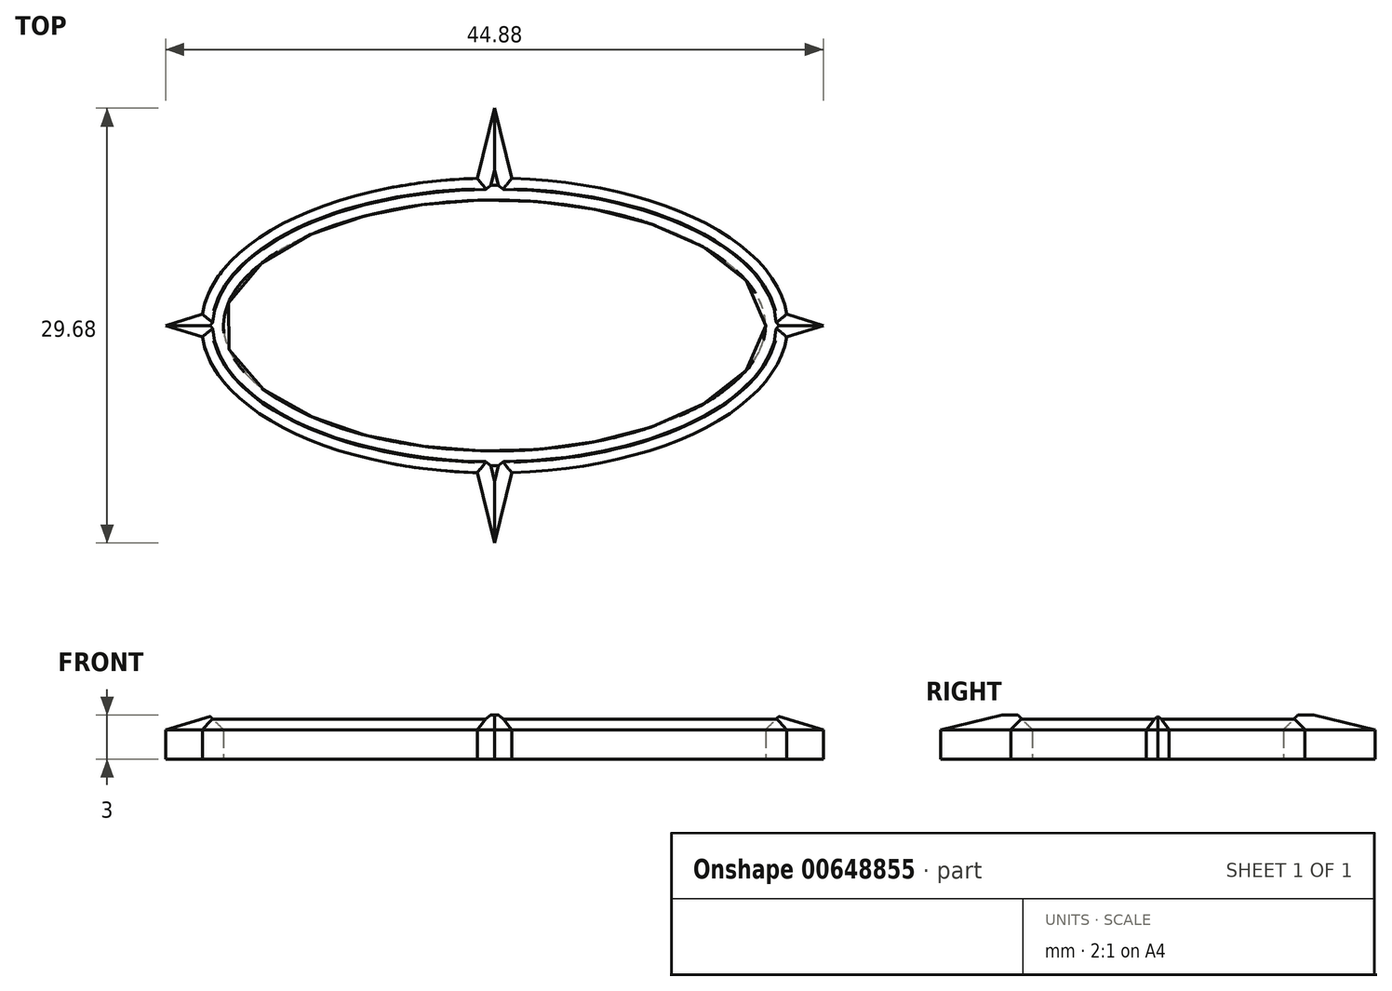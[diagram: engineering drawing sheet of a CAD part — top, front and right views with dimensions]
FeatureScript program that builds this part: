
annotation { "Feature Type Name" : "Feature", "Feature Type Description" : "" }
export const myFeature = defineFeature(function(context is Context, id is Id, definition is map)
    precondition{}
    {
        {
            var Q0;
            Q0=qCreatedBy(makeId("Top.planeOp"),FACE);
            var sketch = newSketch(context, id + "F0", { "sketchPlane" : qUnion([Q0])});
            skEllipse(sketch, "E0", {"center": v(0, 0) * mm, "majorRadius": 20 * mm, "minorRadius": 10.06 * mm, "majorAxis": v(-1, 0)});
            skSolve(sketch);
        }
        {
            var Q0;
            Q0=makeQuery(id+"F0.imprint","IMPRINT",FACE,{"disambiguationData":[TD([[makeQuery(id+"F0.imprint","IMPRINT",EDGE,{"derivedFrom":sQuery(id+"F0.wireOp",EDGE,"E0")}),1.0]])]});
            extrude(context, id + "F1", {"entities" : qUnion([Q0]), "depth" : 3 * mm, "offsetDistance" : 25 * mm});
        }
        {
            var Q0;
            Q0=makeQuery(id+"F1.opExtrude","CAP_FACE",FACE,{"disambiguationData":[OSD([sQuery(id+"F0.wireOp",EDGE,"E0")])],"isStart":false});
            shell(context, id + "F2", {"entities" : qUnion([Q0]), "thickness" : 1.5 * mm});
        }
        {
            var Q0;
            {var subQ0=sQuery(id+"F0.wireOp",EDGE,"E0");Q0=makeQuery(id+"F2.opShell","OFFSET_FACE",FACE,{"disambiguationData":[OSD([subQ0]),TDD([makeQuery(id+"F1.opExtrude","CAP_FACE",FACE,{"disambiguationData":[OSD([subQ0])],"isStart":true})])]});}
            extrude(context, id + "F3", {"entities" : qUnion([Q0]), "operationType" : NewBodyOperationType.REMOVE, "oppositeDirection" : true, "depth" : 25 * mm, "offsetDistance" : 25 * mm});
        }
        {
            var Q0;
            Q0=qCreatedBy(makeId("Top.planeOp"),FACE);
            var sketch = newSketch(context, id + "F4", { "sketchPlane" : qUnion([Q0])});
            skLineSegment(sketch, "E1", {"start": v(0, 9.84) * mm, "end": v(0, 14.84) * mm});
            skLineSegment(sketch, "E2", {"start": v(0, 14.84) * mm, "end": v(-1.22, 9.84) * mm});
            skLineSegment(sketch, "E3", {"start": v(-1.22, 9.84) * mm, "end": v(0, 9.84) * mm});
            skSolve(sketch);
        }
        {
            var Q0;
            Q0=makeQuery(id+"F4.imprint","IMPRINT",FACE,{"disambiguationData":[TD([[makeQuery(id+"F4.imprint","IMPRINT",EDGE,{"derivedFrom":sQuery(id+"F4.wireOp",EDGE,"E1")}),1.0]])]});
            extrude(context, id + "F5", {"entities" : qUnion([Q0]), "operationType" : NewBodyOperationType.ADD, "depth" : 3 * mm, "offsetDistance" : 25 * mm});
        }
        {
            var Q0;
            Q0=qCreatedBy(makeId("Top.planeOp"),FACE);
            var sketch = newSketch(context, id + "F6", { "sketchPlane" : qUnion([Q0])});
            skLineSegment(sketch, "E4", {"start": v(-19.97, 0) * mm, "end": v(-22.44, 0) * mm});
            skLineSegment(sketch, "E5", {"start": v(-22.44, 0) * mm, "end": v(-19.85, 0.8) * mm});
            skLineSegment(sketch, "E6", {"start": v(-19.85, 0.8) * mm, "end": v(-19.97, 0) * mm});
            skSolve(sketch);
        }
        {
            var Q0;
            Q0=makeQuery(id+"F6.imprint","IMPRINT",FACE,{"disambiguationData":[TD([[makeQuery(id+"F6.imprint","IMPRINT",EDGE,{"derivedFrom":sQuery(id+"F6.wireOp",EDGE,"E4")}),-1.0]])]});
            extrude(context, id + "F7", {"entities" : qUnion([Q0]), "operationType" : NewBodyOperationType.ADD, "depth" : 3 * mm, "offsetDistance" : 25 * mm});
        }
        {
            var Q0;
            Q0=makeQuery(id+"F1.opExtrude","SWEPT_BODY",BODY,{"disambiguationData":[OSD([sQuery(id+"F0.wireOp",EDGE,"E0")])]});
            var Q1;
            Q1=qCreatedBy(makeId("Right.planeOp"),FACE);
            mirror(context, id + "F8", {"operationType" : NewBodyOperationType.ADD, "entities" : qUnion([Q0]), "mirrorPlane" : qUnion([Q1])});
        }
        {
            var Q0;
            Q0=makeQuery(id+"F1.opExtrude","SWEPT_BODY",BODY,{"disambiguationData":[OSD([sQuery(id+"F0.wireOp",EDGE,"E0")])]});
            var Q1;
            Q1=qCreatedBy(makeId("Front.planeOp"),FACE);
            mirror(context, id + "F9", {"operationType" : NewBodyOperationType.ADD, "entities" : qUnion([Q0]), "mirrorPlane" : qUnion([Q1])});
        }
        {
            var Q0;
            {var subQ0=sQuery(id+"F4.wireOp",EDGE,"E2");var subQ1=sQuery(id+"F4.wireOp",EDGE,"E1");var subQ4=sQuery(id+"F6.wireOp",EDGE,"E4");var subQ6=sQuery(id+"F0.wireOp",EDGE,"E0");var subQ11=makeQuery(id+"F7.opExtrude","SWEPT_FACE",FACE,{"disambiguationData":[OSD([subQ4])]});Q0=makeQuery(id+"F9.boolean.opBoolean","SPLIT",EDGE,{"disambiguationData":[TD([makeQuery(id+"F9.opPattern","COPY",FACE,{"derivedFrom":makeQuery(id+"F8.opPattern","COPY",FACE,{"derivedFrom":makeQuery(id+"F5.opExtrude","SWEPT_FACE",FACE,{"disambiguationData":[OSD([subQ0])]}),"instanceName":"1"}),"instanceName":"1"})])],"derivedFrom":makeQuery(id+"F8.boolean.opBoolean","SPLIT",EDGE,{"disambiguationData":[TD([subQ11])],"derivedFrom":makeQuery(id+"F7.boolean.opBoolean","SPLIT",EDGE,{"disambiguationData":[TD([makeQuery(id+"F5.opExtrude","SWEPT_FACE",FACE,{"disambiguationData":[OSD([subQ1])]})])],"derivedFrom":makeQuery(id+"F1.opExtrude","CAP_EDGE",EDGE,{"disambiguationData":[OSD([subQ6])],"isStart":false})})})});}
            chamfer(context, id + "F10", {"entities" : qUnion([Q0]), "width" : 1 * mm, "tangentPropagation" : true});
        }
        {
            var Q0;
            {var subQ0=sQuery(id+"F4.wireOp",EDGE,"E2");var subQ1=sQuery(id+"F0.wireOp",EDGE,"E0");Q0=makeQuery(id+"F7.boolean.opBoolean","SPLIT",EDGE,{"disambiguationData":[TD([makeQuery(id+"F5.opExtrude","SWEPT_FACE",FACE,{"disambiguationData":[OSD([subQ0])]})])],"derivedFrom":makeQuery(id+"F1.opExtrude","CAP_EDGE",EDGE,{"disambiguationData":[OSD([subQ1])],"isStart":false})});}
            chamfer(context, id + "F11", {"entities" : qUnion([Q0]), "width" : 1 * mm, "tangentPropagation" : true});
        }
        {
            var Q0;
            {var subQ0=sQuery(id+"F4.wireOp",EDGE,"E2");var subQ1=sQuery(id+"F4.wireOp",EDGE,"E1");var subQ4=sQuery(id+"F6.wireOp",EDGE,"E4");var subQ6=sQuery(id+"F0.wireOp",EDGE,"E0");var subQ11=makeQuery(id+"F7.opExtrude","SWEPT_FACE",FACE,{"disambiguationData":[OSD([subQ4])]});Q0=makeQuery(id+"F9.boolean.opBoolean","SPLIT",EDGE,{"disambiguationData":[TD([makeQuery(id+"F9.opPattern","COPY",FACE,{"derivedFrom":makeQuery(id+"F5.opExtrude","SWEPT_FACE",FACE,{"disambiguationData":[OSD([subQ0])]}),"instanceName":"1"})])],"derivedFrom":makeQuery(id+"F8.boolean.opBoolean","SPLIT",EDGE,{"disambiguationData":[TD([subQ11])],"derivedFrom":makeQuery(id+"F7.boolean.opBoolean","SPLIT",EDGE,{"disambiguationData":[TD([makeQuery(id+"F5.opExtrude","SWEPT_FACE",FACE,{"disambiguationData":[OSD([subQ1])]})])],"derivedFrom":makeQuery(id+"F1.opExtrude","CAP_EDGE",EDGE,{"disambiguationData":[OSD([subQ6])],"isStart":false})})})});}
            chamfer(context, id + "F12", {"entities" : qUnion([Q0]), "width" : 1 * mm, "tangentPropagation" : true});
        }
        {
            var Q0;
            {var subQ0=sQuery(id+"F4.wireOp",EDGE,"E2");var subQ1=sQuery(id+"F4.wireOp",EDGE,"E1");var subQ6=sQuery(id+"F0.wireOp",EDGE,"E0");Q0=makeQuery(id+"F8.boolean.opBoolean","SPLIT",EDGE,{"disambiguationData":[TD([makeQuery(id+"F8.opPattern","COPY",FACE,{"derivedFrom":makeQuery(id+"F5.opExtrude","SWEPT_FACE",FACE,{"disambiguationData":[OSD([subQ0])]}),"instanceName":"1"})])],"derivedFrom":makeQuery(id+"F7.boolean.opBoolean","SPLIT",EDGE,{"disambiguationData":[TD([makeQuery(id+"F5.opExtrude","SWEPT_FACE",FACE,{"disambiguationData":[OSD([subQ1])]})])],"derivedFrom":makeQuery(id+"F1.opExtrude","CAP_EDGE",EDGE,{"disambiguationData":[OSD([subQ6])],"isStart":false})})});}
            chamfer(context, id + "F13", {"entities" : qUnion([Q0]), "width" : 1 * mm, "tangentPropagation" : true});
        }
        {
            var Q0;
            {var subQ0=makeQuery(id+"F7.boolean.opBoolean","MERGE",FACE,{"derivedFrom":[makeQuery(id+"F5.boolean.opBoolean","MERGE",FACE,{"derivedFrom":[makeQuery(id+"F1.opExtrude","CAP_FACE",FACE,{"disambiguationData":[OSD([sQuery(id+"F0.wireOp",EDGE,"E0")])],"isStart":false}),makeQuery(id+"F5.opExtrude","CAP_FACE",FACE,{"disambiguationData":[OSD([sQuery(id+"F4.wireOp",EDGE,"E1"),sQuery(id+"F4.wireOp",EDGE,"E2"),sQuery(id+"F4.wireOp",EDGE,"E3")])],"isStart":false})]}),makeQuery(id+"F7.opExtrude","CAP_FACE",FACE,{"disambiguationData":[OSD([sQuery(id+"F6.wireOp",EDGE,"E4"),sQuery(id+"F6.wireOp",EDGE,"E5"),sQuery(id+"F6.wireOp",EDGE,"E6")])],"isStart":false})]});var subQ1=makeQuery(id+"F8.boolean.opBoolean","MERGE",FACE,{"derivedFrom":[subQ0,makeQuery(id+"F8.opPattern","COPY",FACE,{"derivedFrom":subQ0,"instanceName":"1"})]});Q0=makeQuery(id+"F9.boolean.opBoolean","MERGE",FACE,{"derivedFrom":[subQ1,makeQuery(id+"F9.opPattern","COPY",FACE,{"derivedFrom":subQ1,"instanceName":"1"})]});}
            chamfer(context, id + "F14", {"entities" : qUnion([Q0]), "width" : 1 * mm, "tangentPropagation" : true});
        }
    });
